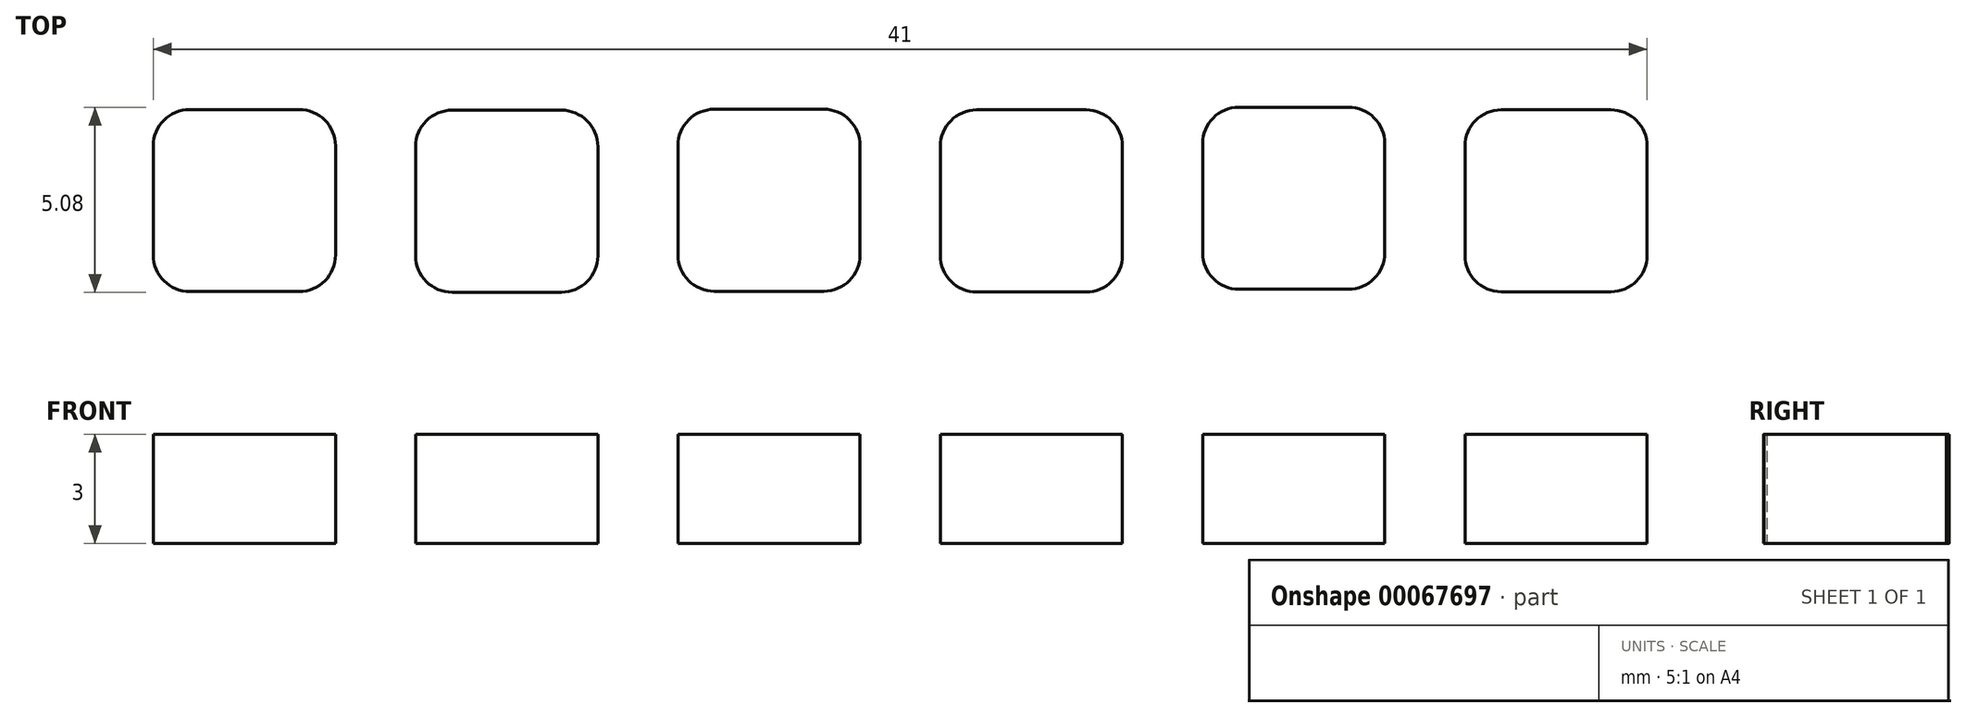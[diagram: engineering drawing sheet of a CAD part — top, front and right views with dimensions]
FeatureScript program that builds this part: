
annotation { "Feature Type Name" : "Feature", "Feature Type Description" : "" }
export const myFeature = defineFeature(function(context is Context, id is Id, definition is map)
    precondition{}
    {
        {
            var Q0;
            Q0=qCreatedBy(makeId("Top.planeOp"),FACE);
            var sketch = newSketch(context, id + "F0", { "sketchPlane" : qUnion([Q0])});
            skLineSegment(sketch, "E0.bottom", {"start": v(-35.72, 12.15) * mm, "end": v(-32.72, 12.15) * mm});
            skLineSegment(sketch, "E0.top", {"start": v(-35.72, 7.15) * mm, "end": v(-32.72, 7.15) * mm});
            skLineSegment(sketch, "E0.left", {"start": v(-36.72, 11.15) * mm, "end": v(-36.72, 8.15) * mm});
            skLineSegment(sketch, "E0.right", {"start": v(-31.72, 11.15) * mm, "end": v(-31.72, 8.15) * mm});
            skPoint(sketch, "E1.visualSharp", {"position": v(-36.72, 12.15) * mm});
            skArc(sketch, "E1.filletArc", {"start": v(-35.72, 12.15) * mm, "mid": v(-36.43, 11.85) * mm, "end": v(-36.72, 11.15) * mm});
            skPoint(sketch, "E2.visualSharp", {"position": v(-31.72, 12.15) * mm});
            skArc(sketch, "E2.filletArc", {"start": v(-31.72, 11.15) * mm, "mid": v(-32.01, 11.85) * mm, "end": v(-32.72, 12.15) * mm});
            skPoint(sketch, "E3.visualSharp", {"position": v(-36.72, 7.15) * mm});
            skArc(sketch, "E3.filletArc", {"start": v(-36.72, 8.15) * mm, "mid": v(-36.43, 7.44) * mm, "end": v(-35.72, 7.15) * mm});
            skPoint(sketch, "E4.visualSharp", {"position": v(-31.72, 7.15) * mm});
            skArc(sketch, "E4.filletArc", {"start": v(-32.72, 7.15) * mm, "mid": v(-32.01, 7.44) * mm, "end": v(-31.72, 8.15) * mm});
            skPoint(sketch, "E5.visualSharp", {"position": v(-10.12, 12.13) * mm});
            skLineSegment(sketch, "E6.bottom", {"start": v(-14.12, 12.13) * mm, "end": v(-11.12, 12.13) * mm});
            skPoint(sketch, "E7.visualSharp", {"position": v(-15.12, 7.13) * mm});
            skLineSegment(sketch, "E6.left", {"start": v(-15.12, 11.13) * mm, "end": v(-15.12, 8.13) * mm});
            skLineSegment(sketch, "E6.top", {"start": v(-14.12, 7.13) * mm, "end": v(-11.12, 7.13) * mm});
            skPoint(sketch, "E8.visualSharp", {"position": v(-10.12, 7.13) * mm});
            skPoint(sketch, "E9.visualSharp", {"position": v(-15.12, 12.13) * mm});
            skLineSegment(sketch, "E6.right", {"start": v(-10.12, 11.13) * mm, "end": v(-10.12, 8.13) * mm});
            skArc(sketch, "E5.filletArc", {"start": v(-10.12, 11.13) * mm, "mid": v(-10.41, 11.84) * mm, "end": v(-11.12, 12.13) * mm});
            skArc(sketch, "E9.filletArc", {"start": v(-14.12, 12.13) * mm, "mid": v(-14.83, 11.84) * mm, "end": v(-15.12, 11.13) * mm});
            skArc(sketch, "E7.filletArc", {"start": v(-15.12, 8.13) * mm, "mid": v(-14.83, 7.43) * mm, "end": v(-14.12, 7.13) * mm});
            skArc(sketch, "E8.filletArc", {"start": v(-11.12, 7.13) * mm, "mid": v(-10.41, 7.43) * mm, "end": v(-10.12, 8.13) * mm});
            skPoint(sketch, "E10.visualSharp", {"position": v(-17.32, 12.2) * mm});
            skLineSegment(sketch, "E11.bottom", {"start": v(-21.32, 12.2) * mm, "end": v(-18.32, 12.2) * mm});
            skPoint(sketch, "E12.visualSharp", {"position": v(-22.32, 7.2) * mm});
            skLineSegment(sketch, "E11.left", {"start": v(-22.32, 11.2) * mm, "end": v(-22.32, 8.2) * mm});
            skLineSegment(sketch, "E11.top", {"start": v(-21.32, 7.2) * mm, "end": v(-18.32, 7.2) * mm});
            skPoint(sketch, "E13.visualSharp", {"position": v(-17.32, 7.2) * mm});
            skPoint(sketch, "E14.visualSharp", {"position": v(-22.32, 12.2) * mm});
            skLineSegment(sketch, "E11.right", {"start": v(-17.32, 11.2) * mm, "end": v(-17.32, 8.2) * mm});
            skArc(sketch, "E10.filletArc", {"start": v(-17.32, 11.2) * mm, "mid": v(-17.61, 11.91) * mm, "end": v(-18.32, 12.2) * mm});
            skArc(sketch, "E14.filletArc", {"start": v(-21.32, 12.2) * mm, "mid": v(-22.03, 11.91) * mm, "end": v(-22.32, 11.2) * mm});
            skArc(sketch, "E12.filletArc", {"start": v(-22.32, 8.2) * mm, "mid": v(-22.03, 7.5) * mm, "end": v(-21.32, 7.2) * mm});
            skArc(sketch, "E13.filletArc", {"start": v(-18.32, 7.2) * mm, "mid": v(-17.61, 7.5) * mm, "end": v(-17.32, 8.2) * mm});
            skPoint(sketch, "E15.visualSharp", {"position": v(-24.52, 12.13) * mm});
            skLineSegment(sketch, "E16.bottom", {"start": v(-28.52, 12.13) * mm, "end": v(-25.52, 12.13) * mm});
            skPoint(sketch, "E17.visualSharp", {"position": v(-29.52, 7.13) * mm});
            skLineSegment(sketch, "E16.left", {"start": v(-29.52, 11.13) * mm, "end": v(-29.52, 8.13) * mm});
            skLineSegment(sketch, "E16.top", {"start": v(-28.52, 7.13) * mm, "end": v(-25.52, 7.13) * mm});
            skPoint(sketch, "E18.visualSharp", {"position": v(-24.52, 7.13) * mm});
            skPoint(sketch, "E19.visualSharp", {"position": v(-29.52, 12.13) * mm});
            skLineSegment(sketch, "E16.right", {"start": v(-24.52, 11.13) * mm, "end": v(-24.52, 8.13) * mm});
            skArc(sketch, "E15.filletArc", {"start": v(-24.52, 11.13) * mm, "mid": v(-24.81, 11.84) * mm, "end": v(-25.52, 12.13) * mm});
            skArc(sketch, "E19.filletArc", {"start": v(-28.52, 12.13) * mm, "mid": v(-29.23, 11.84) * mm, "end": v(-29.52, 11.13) * mm});
            skArc(sketch, "E17.filletArc", {"start": v(-29.52, 8.13) * mm, "mid": v(-29.23, 7.42) * mm, "end": v(-28.52, 7.13) * mm});
            skArc(sketch, "E18.filletArc", {"start": v(-25.52, 7.13) * mm, "mid": v(-24.81, 7.42) * mm, "end": v(-24.52, 8.13) * mm});
            skLineSegment(sketch, "E20.left", {"start": v(-51.12, 11.14) * mm, "end": v(-51.12, 8.14) * mm});
            skLineSegment(sketch, "E21.top", {"start": v(-42.92, 7.12) * mm, "end": v(-39.92, 7.12) * mm});
            skPoint(sketch, "E22.visualSharp", {"position": v(-38.92, 7.12) * mm});
            skPoint(sketch, "E23.visualSharp", {"position": v(-43.92, 12.12) * mm});
            skPoint(sketch, "E24.visualSharp", {"position": v(-43.92, 7.12) * mm});
            skLineSegment(sketch, "E21.bottom", {"start": v(-42.92, 12.12) * mm, "end": v(-39.92, 12.12) * mm});
            skLineSegment(sketch, "E21.right", {"start": v(-38.92, 11.12) * mm, "end": v(-38.92, 8.12) * mm});
            skLineSegment(sketch, "E20.right", {"start": v(-46.12, 11.14) * mm, "end": v(-46.12, 8.14) * mm});
            skPoint(sketch, "E25.visualSharp", {"position": v(-46.12, 7.14) * mm});
            skLineSegment(sketch, "E21.left", {"start": v(-43.92, 11.12) * mm, "end": v(-43.92, 8.12) * mm});
            skLineSegment(sketch, "E20.bottom", {"start": v(-50.12, 12.14) * mm, "end": v(-47.12, 12.14) * mm});
            skLineSegment(sketch, "E20.top", {"start": v(-50.12, 7.14) * mm, "end": v(-47.12, 7.14) * mm});
            skPoint(sketch, "E26.visualSharp", {"position": v(-51.12, 7.14) * mm});
            skPoint(sketch, "E27.visualSharp", {"position": v(-46.12, 12.14) * mm});
            skPoint(sketch, "E28.visualSharp", {"position": v(-51.12, 12.14) * mm});
            skPoint(sketch, "E29.visualSharp", {"position": v(-38.92, 12.12) * mm});
            skArc(sketch, "E23.filletArc", {"start": v(-42.92, 12.12) * mm, "mid": v(-43.63, 11.83) * mm, "end": v(-43.92, 11.12) * mm});
            skArc(sketch, "E29.filletArc", {"start": v(-38.92, 11.12) * mm, "mid": v(-39.21, 11.83) * mm, "end": v(-39.92, 12.12) * mm});
            skArc(sketch, "E25.filletArc", {"start": v(-47.12, 7.14) * mm, "mid": v(-46.41, 7.43) * mm, "end": v(-46.12, 8.14) * mm});
            skArc(sketch, "E22.filletArc", {"start": v(-39.92, 7.12) * mm, "mid": v(-39.21, 7.41) * mm, "end": v(-38.92, 8.12) * mm});
            skArc(sketch, "E28.filletArc", {"start": v(-50.12, 12.14) * mm, "mid": v(-50.83, 11.85) * mm, "end": v(-51.12, 11.14) * mm});
            skArc(sketch, "E24.filletArc", {"start": v(-43.92, 8.12) * mm, "mid": v(-43.63, 7.41) * mm, "end": v(-42.92, 7.12) * mm});
            skArc(sketch, "E26.filletArc", {"start": v(-51.12, 8.14) * mm, "mid": v(-50.83, 7.43) * mm, "end": v(-50.12, 7.14) * mm});
            skArc(sketch, "E27.filletArc", {"start": v(-46.12, 11.14) * mm, "mid": v(-46.41, 11.85) * mm, "end": v(-47.12, 12.14) * mm});
            skSolve(sketch);
        }
        {
            var Q0;
            Q0 = qSketchRegion(id + "F0", true);
            extrude(context, id + "F1", {"entities" : qUnion([Q0]), "depth" : 3 * mm});
        }
    });
